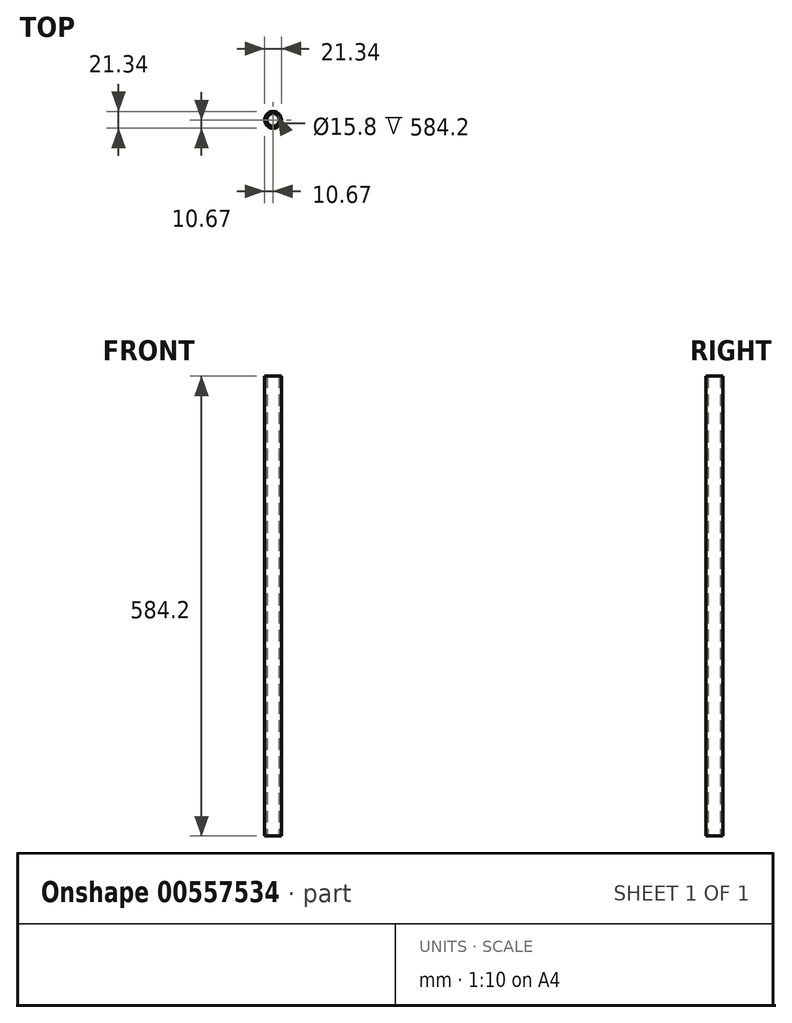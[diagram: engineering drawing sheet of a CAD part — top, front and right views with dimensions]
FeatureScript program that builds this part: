
annotation { "Feature Type Name" : "Feature", "Feature Type Description" : "" }
export const myFeature = defineFeature(function(context is Context, id is Id, definition is map)
    precondition{}
    {
        {
            var Q0;
            Q0=qCreatedBy(makeId("Top.planeOp"),FACE);
            var sketch = newSketch(context, id + "F0", { "sketchPlane" : qUnion([Q0])});
            skCircle(sketch, "E0", {"center": v(0, 0) * mm, "radius": 10.67 * mm});
            skCircle(sketch, "E1", {"center": v(0, 0) * mm, "radius": 7.9 * mm});
            skSolve(sketch);
        }
        {
            var Q0;
            Q0=makeQuery(id+"F0.imprint","IMPRINT",FACE,{"disambiguationData":[TD([[makeQuery(id+"F0.imprint","IMPRINT",EDGE,{"derivedFrom":sQuery(id+"F0.wireOp",EDGE,"E0")}),1.0]])]});
            extrude(context, id + "F1", {"entities" : qUnion([Q0]), "depth" : 584.2 * mm, "offsetDistance" : 25.4 * mm});
        }
    });
